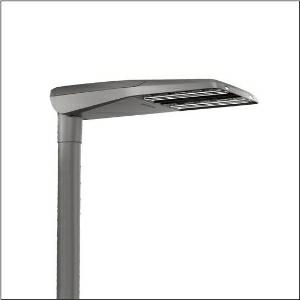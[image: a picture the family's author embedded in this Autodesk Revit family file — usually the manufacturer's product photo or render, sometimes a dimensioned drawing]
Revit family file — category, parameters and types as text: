
# Revit family: streetlight_sl_11_iq_midi___st1_2a_5xc3a51f08me_8c89
name_source: partatom
category: Lighting Fixtures
units: mm (PartAtom-declared; Revit-internal decimal feet)

## family parameters
Cut with Voids When Loaded = No
Host = Face
Light Source = No
Part Type = Normal
Room Calculation Point = No
Round Connector Dimension = Use Diameter
Shared = No

## types (1)
- --- (1 x LED, 18110 lm, 124.7 W, 3000K)
    Apparent Load = 125 VA
    CIE Flux Codes = 32 70 96 100 100
    Color Rendering = 70
    Color Temperature = 3000K
    Default Elevation = 1800 mm
    Description = Streetlight SL 11 iQ midi, mast luminaire, primary light control with 3 zone facetted reflector, of plastic, silver coated, highly specular, primary optical cover: cover, of PMMA, transparent, light distribution: ST1.2a, light emission: direct distribution, primary light characteristic: asymmetric, installation type: post-top, side-entry, lamps: LED, High Power LED, rated values: 18.110lm | 124,7W | 145,2lm/W (begin service life); end service life: 18.110lm | 132,2W; at 50% lumin. flux: 9.055lm | 57,2W | 158,3lm/W, colour temperature: 3000K, colour rendering: CRI > 70, light colour: 730, light setting 1 begin service life: 100% | 18.110lm | 124,7W | 145,2lm/W | 3.000K, light setting 1 end service life: 132,2W, further light settings possible, control: Street-Remote, optimised constant luminous flux control (CLO 2.0), Desk-Remote (wireless, voltage-free reading and setting of iQ features in the workshop via application-optimized NFC function/RFID function), Light-Fading, Smart-Wire, Night-Set, Lumen-Switch, Temp-Guard, Auto-Match, with cable H07RN-F 3x 1.5mm², mains connection: 230..240V, AC, 50/60Hz, connection cable pre-assembled, cable length: 12,5m, luminaire housing, of diecast aluminium, powder-coated, SITECO metallic grey (DB 702S), please order mast flange separately, inclination adjustable without tools: 0°, 5°, 10°, 15° (post-top) | 0°, -5°, -10°, -15° (side-entry), sealing non-destructively replaceable, multi-level sealing system, length: 780mm, width: 376mm, height: 118mm, mast flange for spigot size: 42mm (side-entry): 5XC10008XM4, 60/48mm (side-entry/post-top): 5XC10108XM2, 76/60mm (side-entry/post-top): 5XC10108XM1, equipment: Power, protection rating (complete): IP66, insulation class (complete): insulation class II (safety insulation), certification: CE, ENEC, ENEC+, VDE, impact resistance: IK10, permissible operating ambient temperature for outdoor applications: -25..+50°C, standard-compliant lighting for roads and squares, Environmental Product Declaration (EPD) tested and certified by an independent institute, packaging unit: 1 piece

Light Distribution: ST1.2a
    Height = 118 mm
    Lamp = 1 x LED
    Lamp Light Flux = 18110 lm
    Lamp Power = 124.7 W
    Lamp count = 1
    Length = 780 mm
    Luminous efficacy = 145 lm/W
    Manufacturer = Siteco
    ModVariant = No
    Model = 5XC3A51F08ME
    Number of Poles = 1
    OnlyDefault = Yes
    Power Factor = 1
    Product Name = Streetlight SL 11 iQ midi | ST1.2a
    Product group = mast luminaire | pylon top
    ProductGroupID = 6100
    Protection Class = Protection class II
    Protection Degree = IP 66
    RLX_Detail_Level = 1
    RLX_Emergency_Light_Flux = 0 lm
    RLX_Emergency_Type = 0
    RLX_Emergency_Type_DB = No
    RlxData = <blob elided: 71041 chars, md5=dad2163b>
    Socket = socket
    Standby Power = 0 W
    System Light Flux = 18110 lm
    System Power = 125 W
    Type Comments = factory setting: luminous flux: 100 % | dim-lin: 254 | 557 mA
    Type Image = l_1005960.jpg
    URL = http://relux.com
    VarID = @adj_193687
    Voltage = 0 V
    Weight = 0.00 kg
    Width = 376 mm

## geometry (parser evidence)
native form markers: Blend x4, Sweep x10
no freeform markers — native parametric forms only
